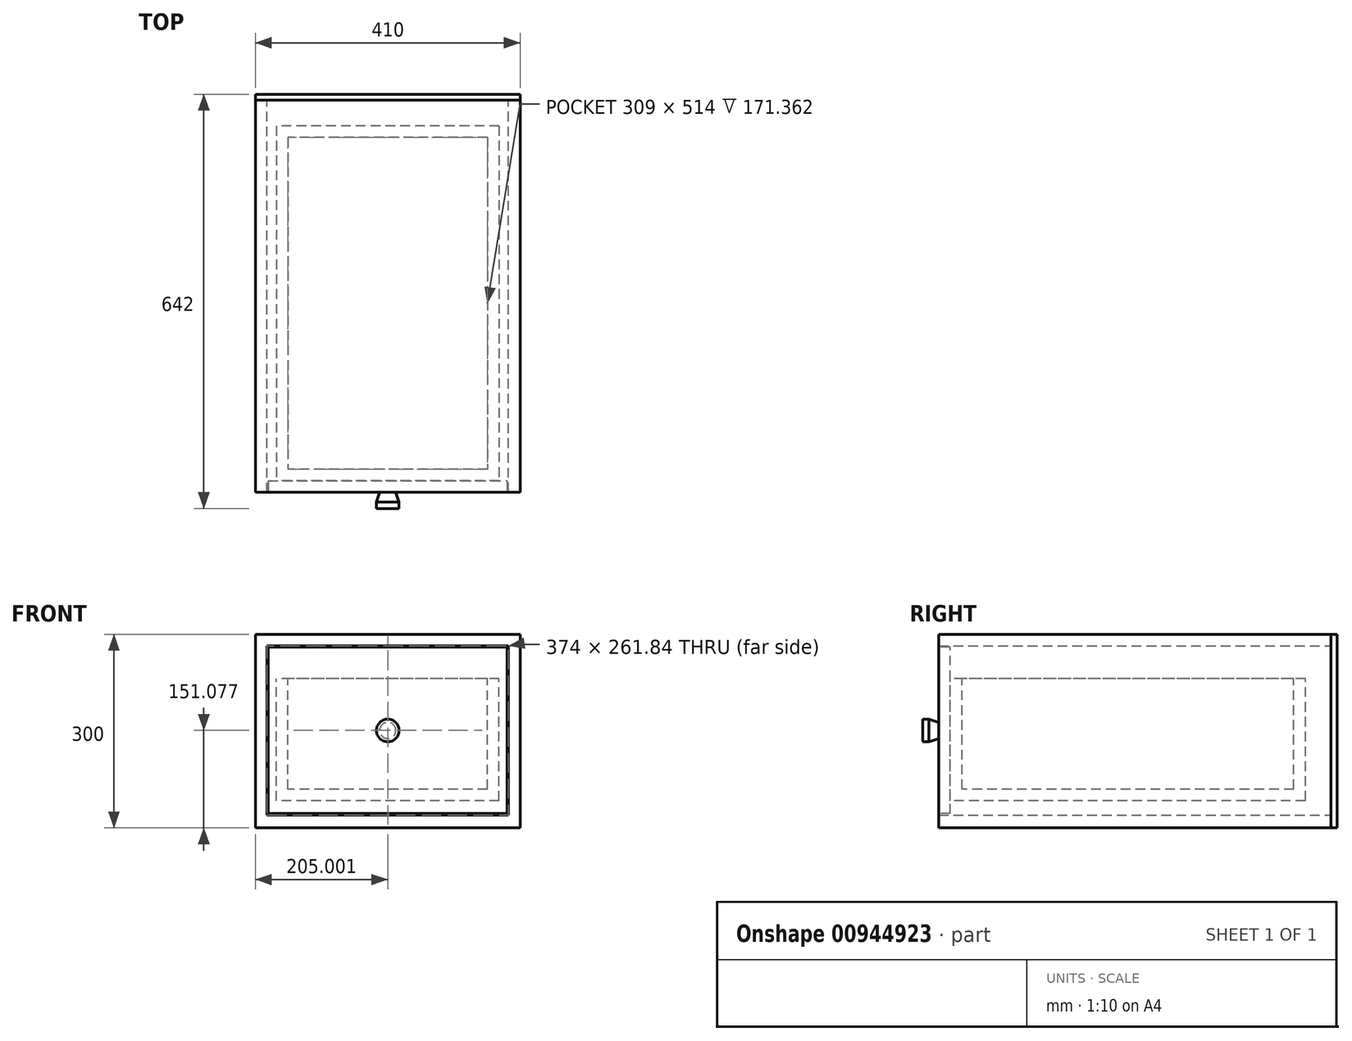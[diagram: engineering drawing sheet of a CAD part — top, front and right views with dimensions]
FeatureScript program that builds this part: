
annotation { "Feature Type Name" : "Feature", "Feature Type Description" : "" }
export const myFeature = defineFeature(function(context is Context, id is Id, definition is map)
    precondition{}
    {
        {
            var Q0;
            Q0=qCreatedBy(makeId("Front.planeOp"),FACE);
            var sketch = newSketch(context, id + "F0", { "sketchPlane" : qUnion([Q0])});
            skLineSegment(sketch, "E0", {"start": v(-326.85, -71.54) * mm, "end": v(-326.85, 228.46) * mm});
            skLineSegment(sketch, "E1.1", {"start": v(-308.85, -51.38) * mm, "end": v(-308.85, 210.46) * mm});
            skLineSegment(sketch, "E2.trimOffspring", {"start": v(65.15, -51.38) * mm, "end": v(-308.85, -51.38) * mm});
            skLineSegment(sketch, "E3.top", {"start": v(-308.85, 210.46) * mm, "end": v(65.15, 210.46) * mm});
            skLineSegment(sketch, "E4.trimOffspring", {"start": v(65.15, 210.46) * mm, "end": v(65.15, -51.38) * mm});
            skLineSegment(sketch, "E5", {"start": v(-326.85, 228.46) * mm, "end": v(83.15, 228.46) * mm});
            skLineSegment(sketch, "E6", {"start": v(83.15, -71.54) * mm, "end": v(83.15, 228.46) * mm});
            skLineSegment(sketch, "E7", {"start": v(-326.85, -71.54) * mm, "end": v(83.15, -71.54) * mm});
            skLineSegment(sketch, "E8.left", {"start": v(83.15, 228.46) * mm, "end": v(83.15, -36.54) * mm, "construction": true});
            skSolve(sketch);
        }
        {
            var Q0;
            Q0=qSketchRegion(id+"F0",true);
            extrude(context, id + "F1", {"entities" : qUnion([Q0]), "depth" : 608 * mm, "offsetDistance" : 25 * mm});
        }
        {
            var Q0;
            Q0=makeQuery(id+"F1.opExtrude","CAP_FACE",FACE,{"disambiguationData":[OSD([sQuery(id+"F0.wireOp",EDGE,"E0"),sQuery(id+"F0.wireOp",EDGE,"1bbb11d5-5f90-4ef2-9ceb-a32cb31813a0"),sQuery(id+"F0.wireOp",EDGE,"E1.1"),sQuery(id+"F0.wireOp",EDGE,"E2.trimOffspring"),sQuery(id+"F0.wireOp",EDGE,"E3.top"),sQuery(id+"F0.wireOp",EDGE,"E4.trimOffspring"),sQuery(id+"F0.wireOp",EDGE,"E5"),sQuery(id+"F0.wireOp",EDGE,"E6")])],"isStart":true});
            var sketch = newSketch(context, id + "F2", { "sketchPlane" : qUnion([Q0])});
            skLineSegment(sketch, "E9.left", {"start": v(-83.15, 228.46) * mm, "end": v(-83.15, 228.46) * mm});
            skLineSegment(sketch, "E9.right", {"start": v(326.85, 228.46) * mm, "end": v(326.85, 228.46) * mm});
            skLineSegment(sketch, "E10.bottom", {"start": v(-83.15, 228.46) * mm, "end": v(326.85, 228.46) * mm});
            skLineSegment(sketch, "E10.top", {"start": v(-83.15, -71.54) * mm, "end": v(326.85, -71.54) * mm});
            skLineSegment(sketch, "E10.left", {"start": v(-83.15, 228.46) * mm, "end": v(-83.15, -71.54) * mm});
            skLineSegment(sketch, "E10.right", {"start": v(326.85, 228.46) * mm, "end": v(326.85, -71.54) * mm});
            skSolve(sketch);
        }
        {
            var Q0;
            Q0=qSketchRegion(id+"F2",true);
            extrude(context, id + "F3", {"entities" : qUnion([Q0]), "depth" : 9 * mm, "offsetDistance" : 25 * mm});
        }
        {
            var Q0;
            Q0=makeQuery(id+"F1.opExtrude","CAP_FACE",FACE,{"disambiguationData":[OSD([sQuery(id+"F0.wireOp",EDGE,"E0"),sQuery(id+"F0.wireOp",EDGE,"1bbb11d5-5f90-4ef2-9ceb-a32cb31813a0"),sQuery(id+"F0.wireOp",EDGE,"E1.1"),sQuery(id+"F0.wireOp",EDGE,"E2.trimOffspring"),sQuery(id+"F0.wireOp",EDGE,"E3.top"),sQuery(id+"F0.wireOp",EDGE,"E4.trimOffspring"),sQuery(id+"F0.wireOp",EDGE,"E5"),sQuery(id+"F0.wireOp",EDGE,"E6")])],"isStart":false});
            var sketch = newSketch(context, id + "F4", { "sketchPlane" : qUnion([Q0])});
            skLineSegment(sketch, "E11.0", {"start": v(-306.85, 208.46) * mm, "end": v(63.15, 208.46) * mm});
            skLineSegment(sketch, "E11.1", {"start": v(-306.85, -49.38) * mm, "end": v(-306.85, 208.46) * mm});
            skLineSegment(sketch, "E11.2", {"start": v(63.15, -49.38) * mm, "end": v(-306.85, -49.38) * mm});
            skLineSegment(sketch, "E11.3", {"start": v(63.15, 208.46) * mm, "end": v(63.15, -49.38) * mm});
            skSolve(sketch);
        }
        {
            var Q0;
            Q0=qSketchRegion(id+"F4",true);
            extrude(context, id + "F5", {"entities" : qUnion([Q0]), "oppositeDirection" : true, "depth" : 18 * mm, "offsetDistance" : 25 * mm});
        }
        {
            var Q0;
            Q0=makeQuery(id+"F5.opExtrude","CAP_FACE",FACE,{"disambiguationData":[OSD([sQuery(id+"F4.wireOp",EDGE,"E11.0"),sQuery(id+"F4.wireOp",EDGE,"E11.1"),sQuery(id+"F4.wireOp",EDGE,"E11.2"),sQuery(id+"F4.wireOp",EDGE,"E11.3")])],"isStart":false});
            var sketch = newSketch(context, id + "F6", { "sketchPlane" : qUnion([Q0])});
            skLineSegment(sketch, "E12.bottom", {"start": v(-50.65, -29.38) * mm, "end": v(294.35, -29.38) * mm});
            skLineSegment(sketch, "E12.top", {"start": v(-50.65, 159.98) * mm, "end": v(294.35, 159.98) * mm});
            skLineSegment(sketch, "E12.left", {"start": v(-50.65, -29.38) * mm, "end": v(-50.65, 159.98) * mm});
            skLineSegment(sketch, "E12.right", {"start": v(294.35, -29.38) * mm, "end": v(294.35, 159.98) * mm});
            skSolve(sketch);
        }
        {
            var Q0;
            Q0=qSketchRegion(id+"F6",true);
            extrude(context, id + "F7", {"entities" : qUnion([Q0]), "depth" : 550 * mm, "offsetDistance" : 25 * mm});
        }
        {
            var Q0;
            Q0=makeQuery(id+"F7.opExtrude","SWEPT_FACE",FACE,{"disambiguationData":[OSD([sQuery(id+"F6.wireOp",EDGE,"E12.top")])]});
            shell(context, id + "F8", {"entities" : qUnion([Q0]), "thickness" : 18 * mm});
        }
        {
            var Q0;
            Q0=makeQuery(id+"F5.opExtrude","CAP_FACE",FACE,{"disambiguationData":[OSD([sQuery(id+"F4.wireOp",EDGE,"E11.0"),sQuery(id+"F4.wireOp",EDGE,"E11.1"),sQuery(id+"F4.wireOp",EDGE,"E11.2"),sQuery(id+"F4.wireOp",EDGE,"E11.3")])],"isStart":true});
            var sketch = newSketch(context, id + "F9", { "sketchPlane" : qUnion([Q0])});
            skLineSegment(sketch, "E13", {"start": v(63.15, 79.54) * mm, "end": v(-306.85, 79.54) * mm, "construction": true});
            skCircle(sketch, "E14", {"center": v(-121.85, 79.54) * mm, "radius": 17.5 * mm});
            skSolve(sketch);
        }
        {
            var Q0;
            Q0=qSketchRegion(id+"F9",true);
            extrude(context, id + "F10", {"entities" : qUnion([Q0]), "depth" : 25 * mm, "offsetDistance" : 25 * mm});
        }
        {
            var Q0;
            Q0=makeQuery(id+"F10.opExtrude","CAP_EDGE",EDGE,{"disambiguationData":[OSD([sQuery(id+"F9.wireOp",EDGE,"E14")])],"isStart":true});
            chamfer(context, id + "F11", {"entities" : qUnion([Q0]), "chamferType" : ChamferType.TWO_OFFSETS, "width1" : 15 * mm, "oppositeDirection" : false, "width2" : 5 * mm, "tangentPropagation" : true});
        }
    });
